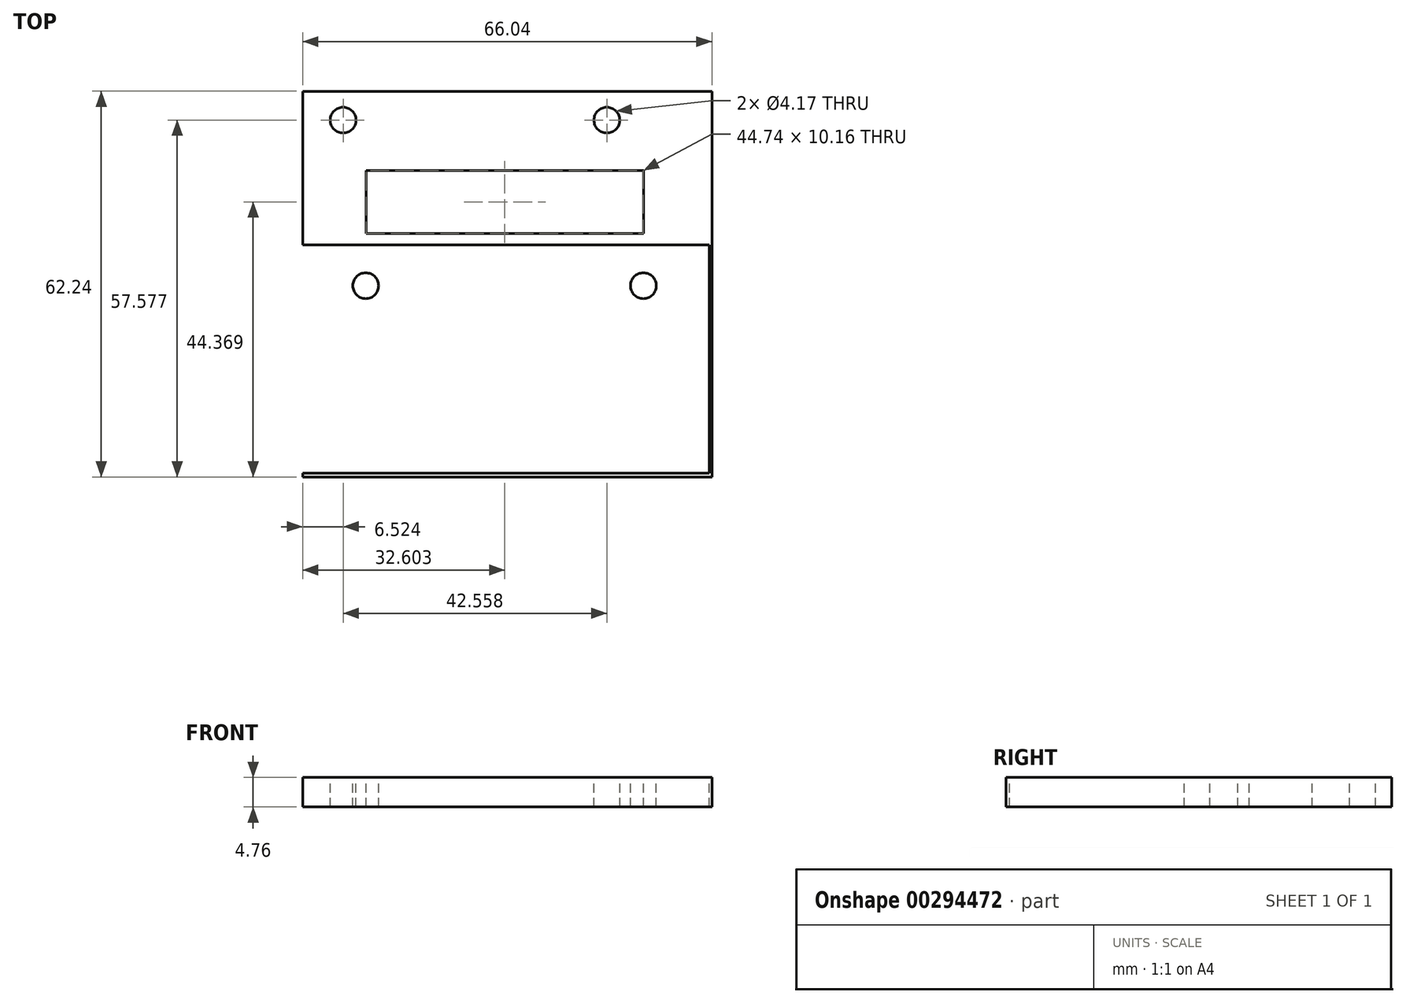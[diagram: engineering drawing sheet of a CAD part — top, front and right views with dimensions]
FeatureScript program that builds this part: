
annotation { "Feature Type Name" : "Feature", "Feature Type Description" : "" }
export const myFeature = defineFeature(function(context is Context, id is Id, definition is map)
    precondition{}
    {
        {
            var Q0;
            Q0=qCreatedBy(makeId("Top.planeOp"),FACE);
            var sketch = newSketch(context, id + "F0", { "sketchPlane" : qUnion([Q0])});
            skLineSegment(sketch, "E0.bottom", {"start": v(33.02, 31.12) * mm, "end": v(-33.02, 31.12) * mm});
            skLineSegment(sketch, "E0.top", {"start": v(33.02, -31.12) * mm, "end": v(-33.02, -31.12) * mm});
            skLineSegment(sketch, "E0.left", {"start": v(33.02, 31.12) * mm, "end": v(33.02, -31.12) * mm});
            skLineSegment(sketch, "E0.right", {"start": v(-33.02, 31.12) * mm, "end": v(-33.02, -31.12) * mm});
            skPoint(sketch, "E0.middle", {"position": v(0, 0) * mm});
            skSolve(sketch);
        }
        {
            var Q0;
            Q0=makeQuery(id+"F0.imprint","IMPRINT",FACE,{"disambiguationData":[TD([[makeQuery(id+"F0.imprint","IMPRINT",EDGE,{"derivedFrom":sQuery(id+"F0.wireOp",EDGE,"E0.bottom")}),1.0]])]});
            extrude(context, id + "F1", {"entities" : qUnion([Q0]), "depth" : 4.76 * mm});
        }
        {
            var Q0;
            Q0=makeQuery(id+"F1.opExtrude","CAP_FACE",FACE,{"disambiguationData":[OSD([sQuery(id+"F0.wireOp",EDGE,"E0.bottom"),sQuery(id+"F0.wireOp",EDGE,"E0.top"),sQuery(id+"F0.wireOp",EDGE,"E0.left"),sQuery(id+"F0.wireOp",EDGE,"E0.right")])],"isStart":false});
            var sketch = newSketch(context, id + "F2", { "sketchPlane" : qUnion([Q0])});
            skLineSegment(sketch, "E1.bottom", {"start": v(32.57, 6.34) * mm, "end": v(-33.47, 6.34) * mm});
            skLineSegment(sketch, "E1.top", {"start": v(32.57, -30.5) * mm, "end": v(-33.47, -30.5) * mm});
            skLineSegment(sketch, "E1.left", {"start": v(32.57, 6.34) * mm, "end": v(32.57, -30.5) * mm});
            skLineSegment(sketch, "E1.right", {"start": v(-33.47, 6.34) * mm, "end": v(-33.47, -30.5) * mm});
            skPoint(sketch, "E1.middle", {"position": v(-0.45, -12.08) * mm});
            skLineSegment(sketch, "E2.bottom", {"start": v(21.95, 6.34) * mm, "end": v(-22.85, 6.34) * mm});
            skLineSegment(sketch, "E2.top", {"start": v(21.95, -30.5) * mm, "end": v(-22.85, -30.5) * mm});
            skLineSegment(sketch, "E2.left", {"start": v(21.95, 6.34) * mm, "end": v(21.95, -30.5) * mm});
            skLineSegment(sketch, "E2.right", {"start": v(-22.85, 6.34) * mm, "end": v(-22.85, -30.5) * mm});
            skCircle(sketch, "E3", {"center": v(21.95, -0.26) * mm, "radius": 2.08 * mm});
            skCircle(sketch, "E4", {"center": v(21.95, -26.43) * mm, "radius": 2.08 * mm});
            skCircle(sketch, "E5", {"center": v(-22.85, -0.26) * mm, "radius": 2.08 * mm});
            skCircle(sketch, "E6", {"center": v(-22.85, -26.43) * mm, "radius": 2.08 * mm});
            skLineSegment(sketch, "E7", {"start": v(-38.55, 8.17) * mm, "end": v(40.2, 8.17) * mm});
            skLineSegment(sketch, "E8.bottom", {"start": v(21.95, 8.17) * mm, "end": v(-22.79, 8.17) * mm});
            skLineSegment(sketch, "E8.top", {"start": v(21.95, 18.33) * mm, "end": v(-22.79, 18.33) * mm});
            skLineSegment(sketch, "E8.left", {"start": v(21.95, 8.17) * mm, "end": v(21.95, 18.33) * mm});
            skLineSegment(sketch, "E8.right", {"start": v(-22.79, 8.17) * mm, "end": v(-22.79, 18.33) * mm});
            skCircle(sketch, "E9", {"center": v(16.06, 26.46) * mm, "radius": 2.08 * mm});
            skCircle(sketch, "E10", {"center": v(-26.5, 26.46) * mm, "radius": 2.08 * mm});
            skLineSegment(sketch, "E11", {"start": v(-26.5, 26.46) * mm, "end": v(16.06, 26.46) * mm});
            skLineSegment(sketch, "E12", {"start": v(0.82, 30.47) * mm, "end": v(0.82, -12.08) * mm});
            skLineSegment(sketch, "E13", {"start": v(21.95, 18.33) * mm, "end": v(21.95, 30.47) * mm});
            skSolve(sketch);
        }
        {
            var Q0;
            Q0=makeQuery(id+"F2.imprint","IMPRINT",FACE,{"disambiguationData":[TD([[makeQuery(id+"F2.imprint","IMPRINT",EDGE,{"derivedFrom":sQuery(id+"F2.wireOp",EDGE,"E10")}),1.0]])]});
            var Q1;
            Q1=makeQuery(id+"F2.imprint","IMPRINT",FACE,{"disambiguationData":[TD([[makeQuery(id+"F2.imprint","IMPRINT",EDGE,{"derivedFrom":sQuery(id+"F2.wireOp",EDGE,"E9")}),1.0]])]});
            var Q2;
            {var subQ0=sQuery(id+"F2.wireOp",EDGE,"E3");var subQ1=sQuery(id+"F2.wireOp",EDGE,"E2.left");var subQ2=makeQuery(id+"F2.imprint","INTERSECT",VERTEX,{"disambiguationData":[OD(0.0)],"derivedFrom":[subQ1,subQ0]});Q2=makeQuery(id+"F2.imprint","IMPRINT",FACE,{"disambiguationData":[TD([[makeQuery(id+"F2.imprint","IMPRINT",EDGE,{"disambiguationData":[TD([[subQ2,-1.0]])],"derivedFrom":subQ1}),1.0]])]});}
            var Q3;
            {var subQ0=sQuery(id+"F2.wireOp",EDGE,"E3");var subQ1=sQuery(id+"F2.wireOp",EDGE,"E2.left");var subQ2=makeQuery(id+"F2.imprint","INTERSECT",VERTEX,{"disambiguationData":[OD(0.0)],"derivedFrom":[subQ1,subQ0]});Q3=makeQuery(id+"F2.imprint","IMPRINT",FACE,{"disambiguationData":[TD([[makeQuery(id+"F2.imprint","IMPRINT",EDGE,{"disambiguationData":[TD([[subQ2,-1.0]])],"derivedFrom":subQ1}),-1.0]])]});}
            var Q4;
            {var subQ0=sQuery(id+"F2.wireOp",EDGE,"E5");var subQ1=sQuery(id+"F2.wireOp",EDGE,"E2.right");var subQ2=makeQuery(id+"F2.imprint","INTERSECT",VERTEX,{"disambiguationData":[OD(0.0)],"derivedFrom":[subQ1,subQ0]});Q4=makeQuery(id+"F2.imprint","IMPRINT",FACE,{"disambiguationData":[TD([[makeQuery(id+"F2.imprint","IMPRINT",EDGE,{"disambiguationData":[TD([[subQ2,-1.0]])],"derivedFrom":subQ1}),1.0]])]});}
            var Q5;
            {var subQ0=sQuery(id+"F2.wireOp",EDGE,"E5");var subQ1=sQuery(id+"F2.wireOp",EDGE,"E2.right");var subQ2=makeQuery(id+"F2.imprint","INTERSECT",VERTEX,{"disambiguationData":[OD(0.0)],"derivedFrom":[subQ1,subQ0]});Q5=makeQuery(id+"F2.imprint","IMPRINT",FACE,{"disambiguationData":[TD([[makeQuery(id+"F2.imprint","IMPRINT",EDGE,{"disambiguationData":[TD([[subQ2,-1.0]])],"derivedFrom":subQ1}),-1.0]])]});}
            var Q6;
            {var subQ0=sQuery(id+"F2.wireOp",EDGE,"E6");var subQ1=sQuery(id+"F2.wireOp",EDGE,"E2.right");var subQ2=makeQuery(id+"F2.imprint","INTERSECT",VERTEX,{"disambiguationData":[OD(0.0)],"derivedFrom":[subQ1,subQ0]});Q6=makeQuery(id+"F2.imprint","IMPRINT",FACE,{"disambiguationData":[TD([[makeQuery(id+"F2.imprint","IMPRINT",EDGE,{"disambiguationData":[TD([[subQ2,-1.0]])],"derivedFrom":subQ1}),1.0]])]});}
            var Q7;
            {var subQ0=sQuery(id+"F2.wireOp",EDGE,"E6");var subQ1=sQuery(id+"F2.wireOp",EDGE,"E2.right");var subQ2=makeQuery(id+"F2.imprint","INTERSECT",VERTEX,{"disambiguationData":[OD(0.0)],"derivedFrom":[subQ1,subQ0]});Q7=makeQuery(id+"F2.imprint","IMPRINT",FACE,{"disambiguationData":[TD([[makeQuery(id+"F2.imprint","IMPRINT",EDGE,{"disambiguationData":[TD([[subQ2,-1.0]])],"derivedFrom":subQ1}),-1.0]])]});}
            var Q8;
            {var subQ0=sQuery(id+"F2.wireOp",EDGE,"E4");var subQ1=sQuery(id+"F2.wireOp",EDGE,"E2.left");var subQ2=makeQuery(id+"F2.imprint","INTERSECT",VERTEX,{"disambiguationData":[OD(0.0)],"derivedFrom":[subQ1,subQ0]});Q8=makeQuery(id+"F2.imprint","IMPRINT",FACE,{"disambiguationData":[TD([[makeQuery(id+"F2.imprint","IMPRINT",EDGE,{"disambiguationData":[TD([[subQ2,-1.0]])],"derivedFrom":subQ1}),1.0]])]});}
            var Q9;
            {var subQ0=sQuery(id+"F2.wireOp",EDGE,"E4");var subQ1=sQuery(id+"F2.wireOp",EDGE,"E2.left");var subQ2=makeQuery(id+"F2.imprint","INTERSECT",VERTEX,{"disambiguationData":[OD(0.0)],"derivedFrom":[subQ1,subQ0]});Q9=makeQuery(id+"F2.imprint","IMPRINT",FACE,{"disambiguationData":[TD([[makeQuery(id+"F2.imprint","IMPRINT",EDGE,{"disambiguationData":[TD([[subQ2,-1.0]])],"derivedFrom":subQ1}),-1.0]])]});}
            var Q10;
            {var subQ0=sQuery(id+"F2.wireOp",EDGE,"E8.right");Q10=makeQuery(id+"F2.imprint","IMPRINT",FACE,{"disambiguationData":[TD([[makeQuery(id+"F2.imprint","IMPRINT",EDGE,{"derivedFrom":subQ0}),-1.0]])]});}
            var Q11;
            {var subQ0=sQuery(id+"F2.wireOp",EDGE,"E8.left");Q11=makeQuery(id+"F2.imprint","IMPRINT",FACE,{"disambiguationData":[TD([[makeQuery(id+"F2.imprint","IMPRINT",EDGE,{"derivedFrom":subQ0}),1.0]])]});}
            extrude(context, id + "F3", {"entities" : qUnion([Q0, Q1, Q2, Q3, Q4, Q5, Q6, Q7, Q8, Q9, Q10, Q11]), "operationType" : NewBodyOperationType.REMOVE, "oppositeDirection" : true, "depth" : 25.4 * mm});
        }
    });
